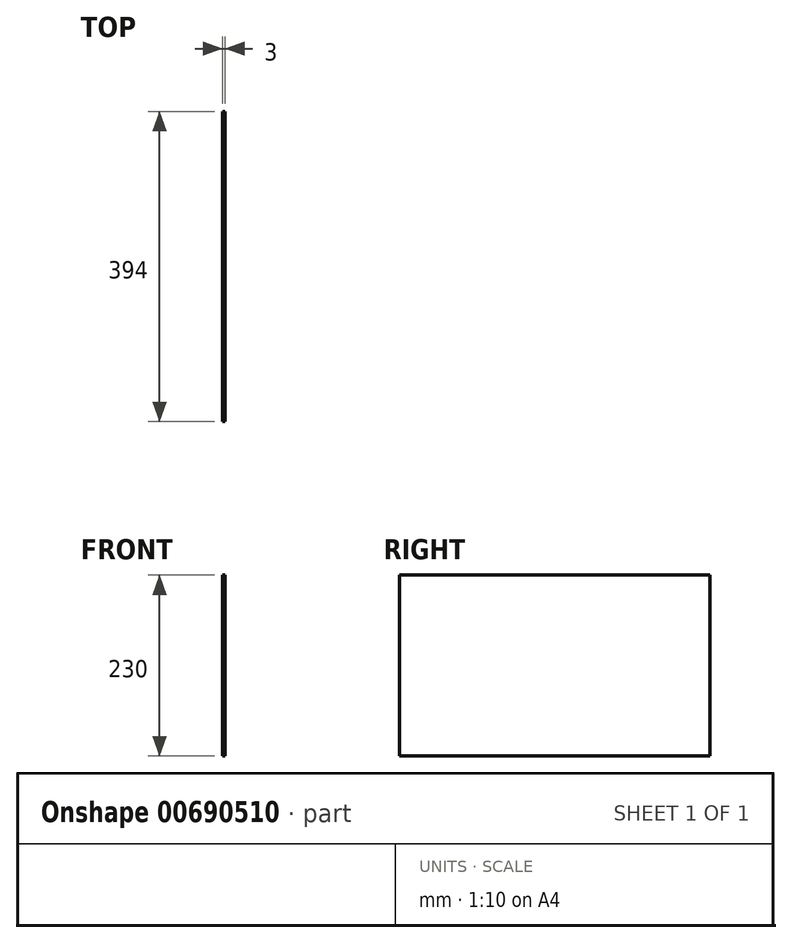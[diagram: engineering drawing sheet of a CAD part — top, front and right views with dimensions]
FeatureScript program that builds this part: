
annotation { "Feature Type Name" : "Feature", "Feature Type Description" : "" }
export const myFeature = defineFeature(function(context is Context, id is Id, definition is map)
    precondition{}
    {
        {
            var Q0;
            Q0=qCreatedBy(makeId("Right.planeOp"),FACE);
            var sketch = newSketch(context, id + "F0", { "sketchPlane" : qUnion([Q0])});
            skLineSegment(sketch, "E0", {"start": v(0, 0) * mm, "end": v(0, 230) * mm});
            skLineSegment(sketch, "E1", {"start": v(0, 0) * mm, "end": v(394, 0) * mm});
            skLineSegment(sketch, "E2", {"start": v(394, 0) * mm, "end": v(394, 230) * mm});
            skLineSegment(sketch, "E3", {"start": v(0, 230) * mm, "end": v(394, 230) * mm});
            skSolve(sketch);
        }
        {
            var Q0;
            Q0=makeQuery(id+"F0.imprint","IMPRINT",FACE,{"disambiguationData":[TD([[makeQuery(id+"F0.imprint","IMPRINT",EDGE,{"derivedFrom":sQuery(id+"F0.wireOp",EDGE,"E0")}),-1.0]])]});
            extrude(context, id + "F1", {"entities" : qUnion([Q0]), "depth" : 3 * mm, "offsetDistance" : 25 * mm});
        }
    });
